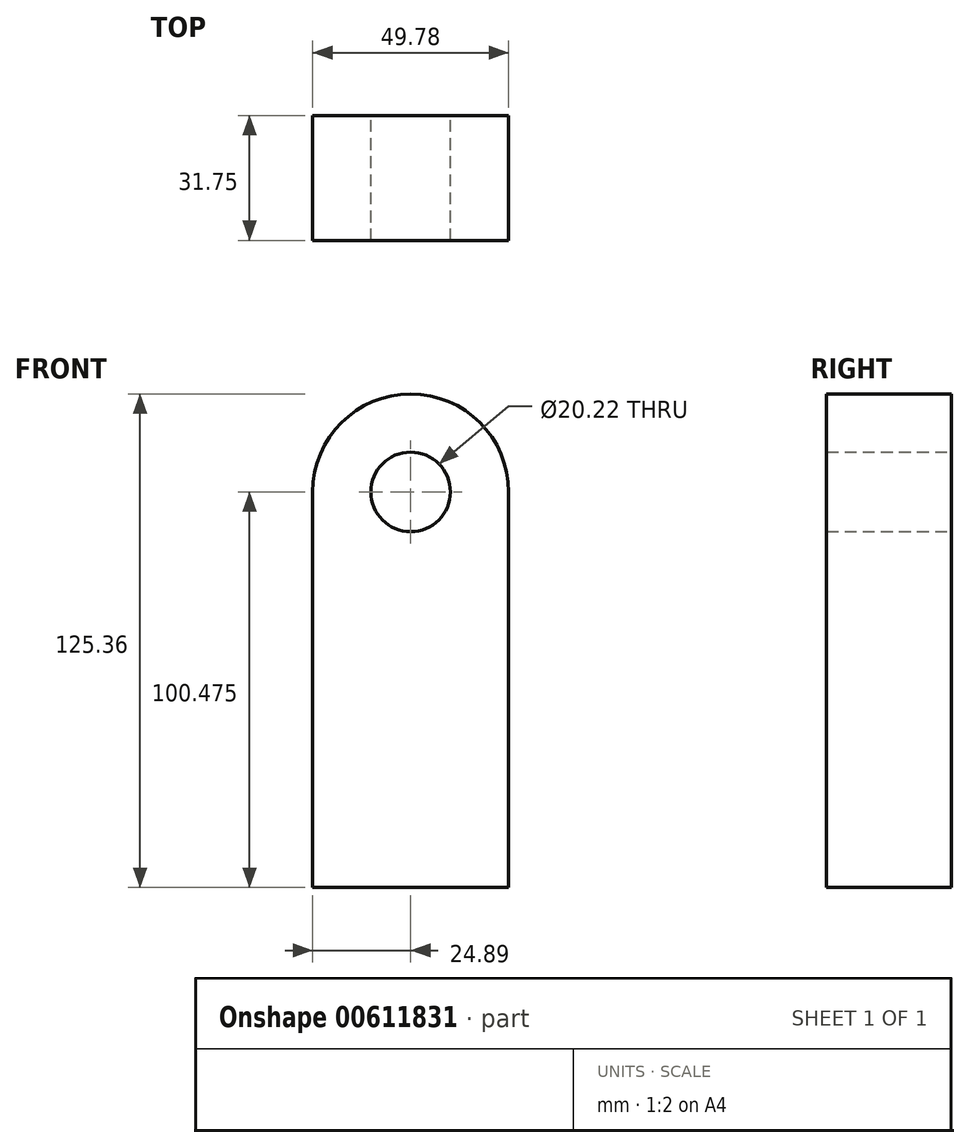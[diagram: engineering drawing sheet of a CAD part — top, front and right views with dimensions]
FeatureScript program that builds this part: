
annotation { "Feature Type Name" : "Feature", "Feature Type Description" : "" }
export const myFeature = defineFeature(function(context is Context, id is Id, definition is map)
    precondition{}
    {
        {
            var Q0;
            Q0=qCreatedBy(makeId("Front.planeOp"),FACE);
            var sketch = newSketch(context, id + "F0", { "sketchPlane" : qUnion([Q0])});
            skLineSegment(sketch, "E0.top", {"start": v(-24.89, -50.24) * mm, "end": v(24.89, -50.24) * mm});
            skLineSegment(sketch, "E0.left", {"start": v(-24.89, 50.24) * mm, "end": v(-24.89, -50.24) * mm});
            skLineSegment(sketch, "E0.right", {"start": v(24.89, 50.24) * mm, "end": v(24.89, -50.24) * mm});
            skPoint(sketch, "E0.middle", {"position": v(0, 0) * mm});
            skCircle(sketch, "E1", {"center": v(0, 50.24) * mm, "radius": 24.89 * mm});
            skCircle(sketch, "E2", {"center": v(0, 50.24) * mm, "radius": 10.11 * mm});
            skSolve(sketch);
        }
        {
            var Q0;
            Q0 = qSketchRegion(id + "F0", true);
            extrude(context, id + "F1", {"entities" : qUnion([Q0]), "depth" : 31.75 * mm, "offsetDistance" : 25.4 * mm});
        }
    });
